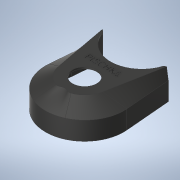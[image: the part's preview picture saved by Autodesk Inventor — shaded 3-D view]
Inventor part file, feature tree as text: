
AUTODESK INVENTOR PART (.ipt)
format: ipt  version: 2020.1 (Build 241239000, 239)  size: 1,566,720 bytes
history: native  units: mm
features: other x17, sketch x6, loft x6, extrude x5, plane x2, chamfer x2, emboss x1
ambient origin geometry x8: Origin, YZ Plane, XZ Plane, XY Plane, X Axis, Y Axis, Z Axis, Center Point
bodies: Body1 (feature_tree), Body2 (feature_tree)
feature tree (39):
  other  "Motor Holder v3 - 225 - ABS.ipt"
  plane  "Work Plane2"
  sketch  "Sketch2"  dims[d0=10.0mm d3=3.5mm]
  plane  "Work Plane1"
  extrude  "Extrusion4"  Depth=3.5mm
  sketch  "3D Sketch1"
  loft  "Loft6"
  extrude  "Extrusion5"  Depth=2.75mm
  extrude  "Extrusion6"  Depth=64.0mm
  loft  "Loft7"
  loft  "Loft8"
  loft  "Loft9"
  loft  "Loft10"
  loft  "Loft11"
  chamfer  "Chamfer3"  Distance=2.0mm
  extrude  "Extrusion7"  Depth=5.0mm TaperAngle=0.0deg
  chamfer  "Chamfer4"  Distance=1.5mm
  extrude  "Extrusion24"  Depth=16.0mm TaperAngle=0.0deg
  emboss  "Emboss1"
  other  "Solid3::Motor Holder v3 - 225 - ABS.ipt"
  other  "TaggingFeature1"
  other  "Holder Cover"
  other  "Edges1"
  other  "Edges2"
  other  "Edges3"
  other  "Edges4"
  other  "Edges5"
  other  "Edges6"
  other  "Edges7"
  other  "Edges8"
  other  "Edges9"
  sketch  "3D Sketch2"
  sketch  "Sketch8"  dims[d4=3.5mm d5=21.0mm]
  sketch  "Sketch24"  dims[d6=2.5mm d14=2.75mm d15=2.75mm]
  sketch  "Sketch28"  dims[d24=-7.25mm d26=64.0mm d28=32.0mm d29=1.5mm d41=0.5mm d43=0.5mm d51=2.0mm d52=2.0mm d67=5.0mm d68=0.0mm d73=1.5mm d74=0.0mm d75=16.0mm d76=0.0mm d81=29.698599mm d88=0.858664mm d91=1.296614mm d92=45.0deg d97=3.5mm d100=3.5mm d103=0.0mm d104=90.0deg d105=0.0mm d106=90.0deg d107=0.0mm d108=90.0deg d109=0.0mm d110=90.0deg d111=0.0mm d112=90.0deg d113=0.0mm d114=90.0deg d115=0.0mm d116=90.0deg d117=0.0mm d118=90.0deg d119=0.0mm d120=90.0deg d121=0.0mm d122=90.0deg d123=0.0mm d124=90.0deg d125=0.0mm d126=90.0deg d127=0.5mm d128=1.5mm d129=45.0deg d130=23.0mm d131=0.0mm d132=0.5mm d133=1.5mm d134=45.0deg d146=2.75mm d170=52.0mm d171=2.0mm d264=2.0mm d267=2.0mm d294=1.452114mm d295=1.452114mm d304=1.452114mm d305=1.452114mm d329=15.0mm d330=0.0mm d331=5.0mm d332=5.0mm d333=5.0mm d335=0.4mm d336=0.0mm d337=0.0mm d338=90.0deg d339=0.0mm d340=90.0deg]
  other  "Edges10"
  other  "Edges11"
  other  "Edges12"
  other  "Holder"
